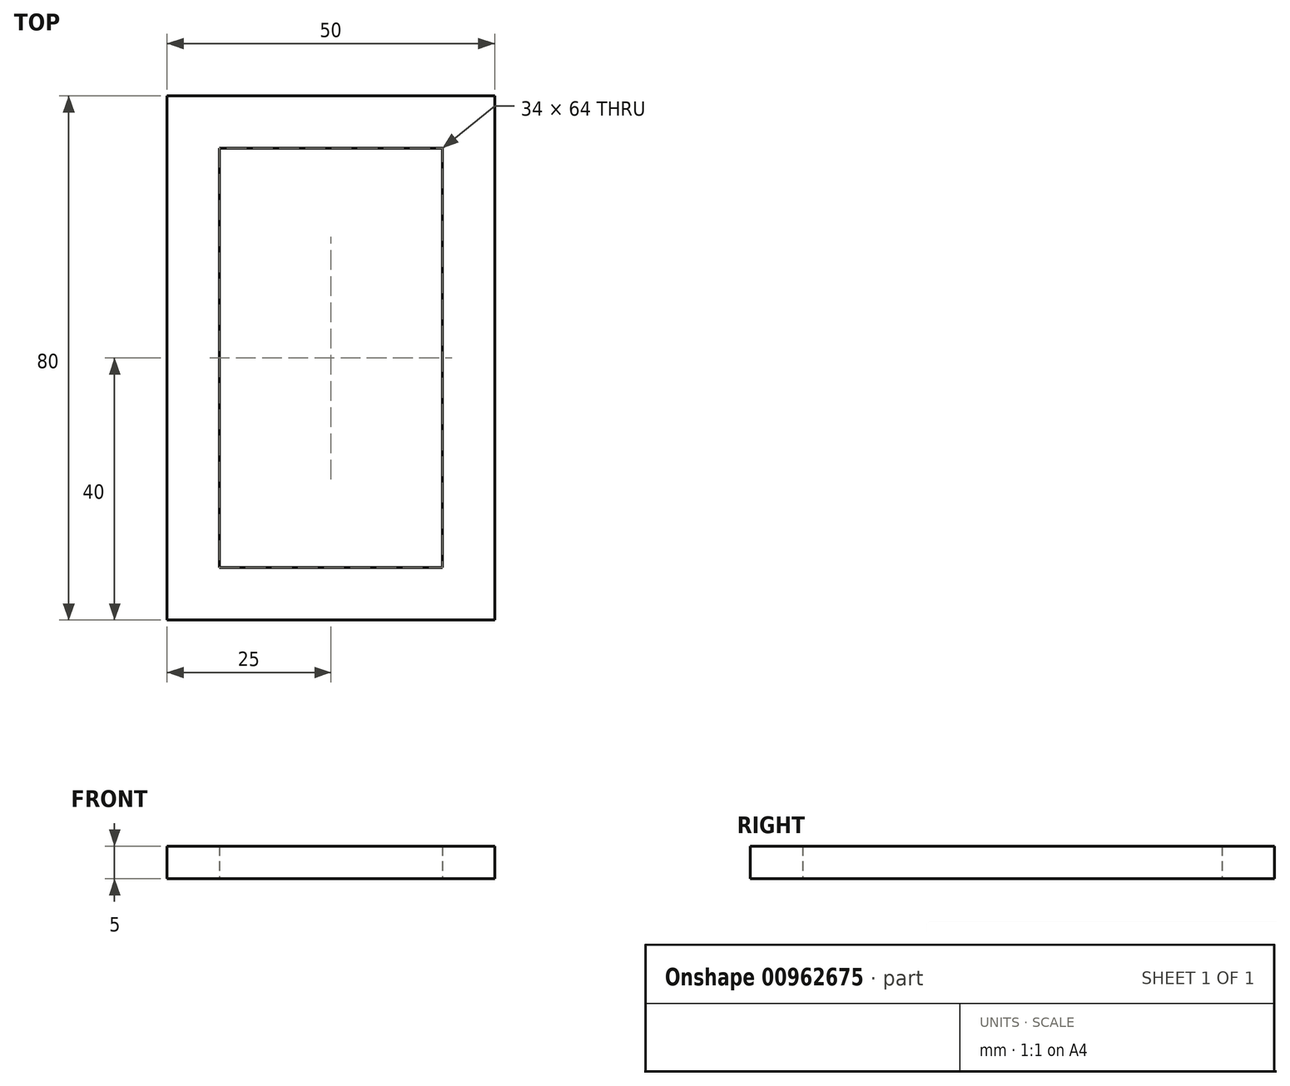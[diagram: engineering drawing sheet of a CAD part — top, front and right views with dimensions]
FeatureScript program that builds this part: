
annotation { "Feature Type Name" : "Feature", "Feature Type Description" : "" }
export const myFeature = defineFeature(function(context is Context, id is Id, definition is map)
    precondition{}
    {
        {
            var Q0;
            Q0=qCreatedBy(makeId("Top.planeOp"),FACE);
            var sketch = newSketch(context, id + "F0", { "sketchPlane" : qUnion([Q0])});
            skLineSegment(sketch, "E0.bottom", {"start": v(0, 0) * mm, "end": v(50, 0) * mm});
            skLineSegment(sketch, "E0.top", {"start": v(0, -80) * mm, "end": v(50, -80) * mm});
            skLineSegment(sketch, "E0.left", {"start": v(0, 0) * mm, "end": v(0, -80) * mm});
            skLineSegment(sketch, "E0.right", {"start": v(50, 0) * mm, "end": v(50, -80) * mm});
            skLineSegment(sketch, "E1.bottom", {"start": v(8, -8) * mm, "end": v(42, -8) * mm});
            skLineSegment(sketch, "E1.top", {"start": v(8, -72) * mm, "end": v(42, -72) * mm});
            skLineSegment(sketch, "E1.left", {"start": v(8, -8) * mm, "end": v(8, -72) * mm});
            skLineSegment(sketch, "E1.right", {"start": v(42, -8) * mm, "end": v(42, -72) * mm});
            skLineSegment(sketch, "E2", {"start": v(8, -72) * mm, "end": v(0, -72) * mm, "construction": true});
            skLineSegment(sketch, "E3", {"start": v(8, -8) * mm, "end": v(8, 0) * mm, "construction": true});
            skLineSegment(sketch, "E4", {"start": v(42, -8) * mm, "end": v(50, -8) * mm, "construction": true});
            skLineSegment(sketch, "E5", {"start": v(42, -72) * mm, "end": v(42, -80) * mm, "construction": true});
            skSolve(sketch);
        }
        {
            var Q0;
            Q0=makeQuery(id+"F0.imprint","IMPRINT",FACE,{"disambiguationData":[TD([[makeQuery(id+"F0.imprint","IMPRINT",EDGE,{"derivedFrom":sQuery(id+"F0.wireOp",EDGE,"E0.bottom")}),-1.0]])]});
            extrude(context, id + "F1", {"entities" : qUnion([Q0]), "depth" : 5 * mm, "offsetDistance" : 25.4 * mm});
        }
    });
